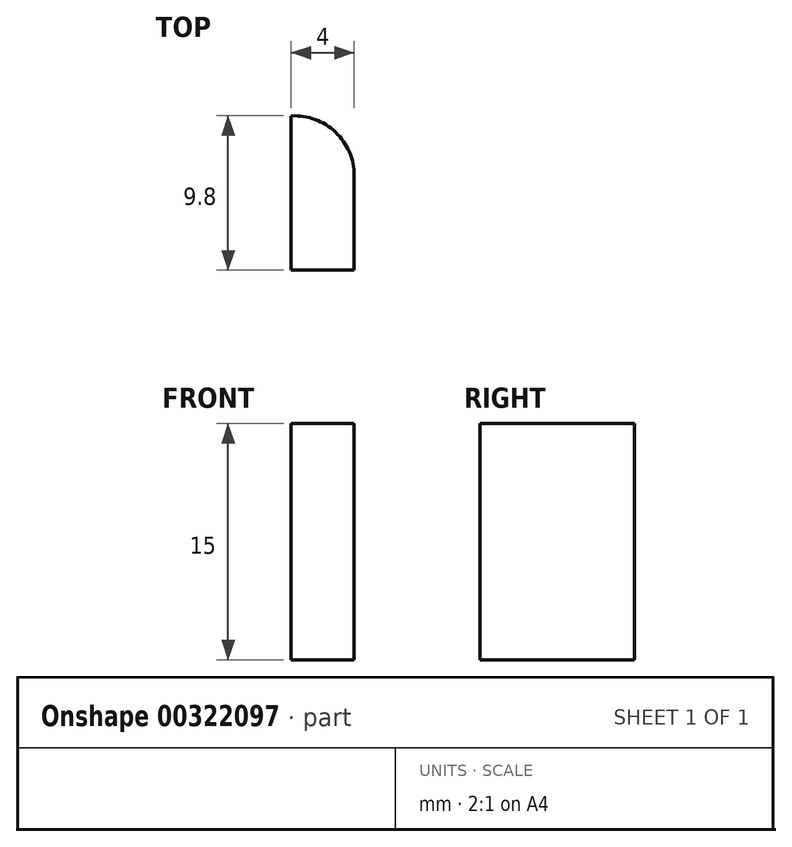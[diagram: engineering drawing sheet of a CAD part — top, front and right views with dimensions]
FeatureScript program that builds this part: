
annotation { "Feature Type Name" : "Feature", "Feature Type Description" : "" }
export const myFeature = defineFeature(function(context is Context, id is Id, definition is map)
    precondition{}
    {
        {
            var Q0;
            Q0=qCreatedBy(makeId("Top.planeOp"),FACE);
            var sketch = newSketch(context, id + "F0", { "sketchPlane" : qUnion([Q0])});
            skLineSegment(sketch, "E0.top", {"start": v(0, -6) * mm, "end": v(4, -6) * mm});
            skLineSegment(sketch, "E0.left", {"start": v(0, 0) * mm, "end": v(0, -6) * mm});
            skLineSegment(sketch, "E0.right", {"start": v(4, 0) * mm, "end": v(4, -6) * mm});
            skArc(sketch, "E1", {"start": v(4, 0) * mm, "mid": v(2.82, 2.76) * mm, "end": v(0, 3.8) * mm});
            skLineSegment(sketch, "E2", {"start": v(0, 0) * mm, "end": v(0, 3.8) * mm});
            skLineSegment(sketch, "E3", {"start": v(0, 3.8) * mm, "end": v(-2.38, 3.67) * mm, "construction": true});
            skSolve(sketch);
        }
        {
            var Q0;
            Q0=qSketchRegion(id+"F0",true);
            extrude(context, id + "F1", {"entities" : qUnion([Q0]), "depth" : 15 * mm});
        }
    });
